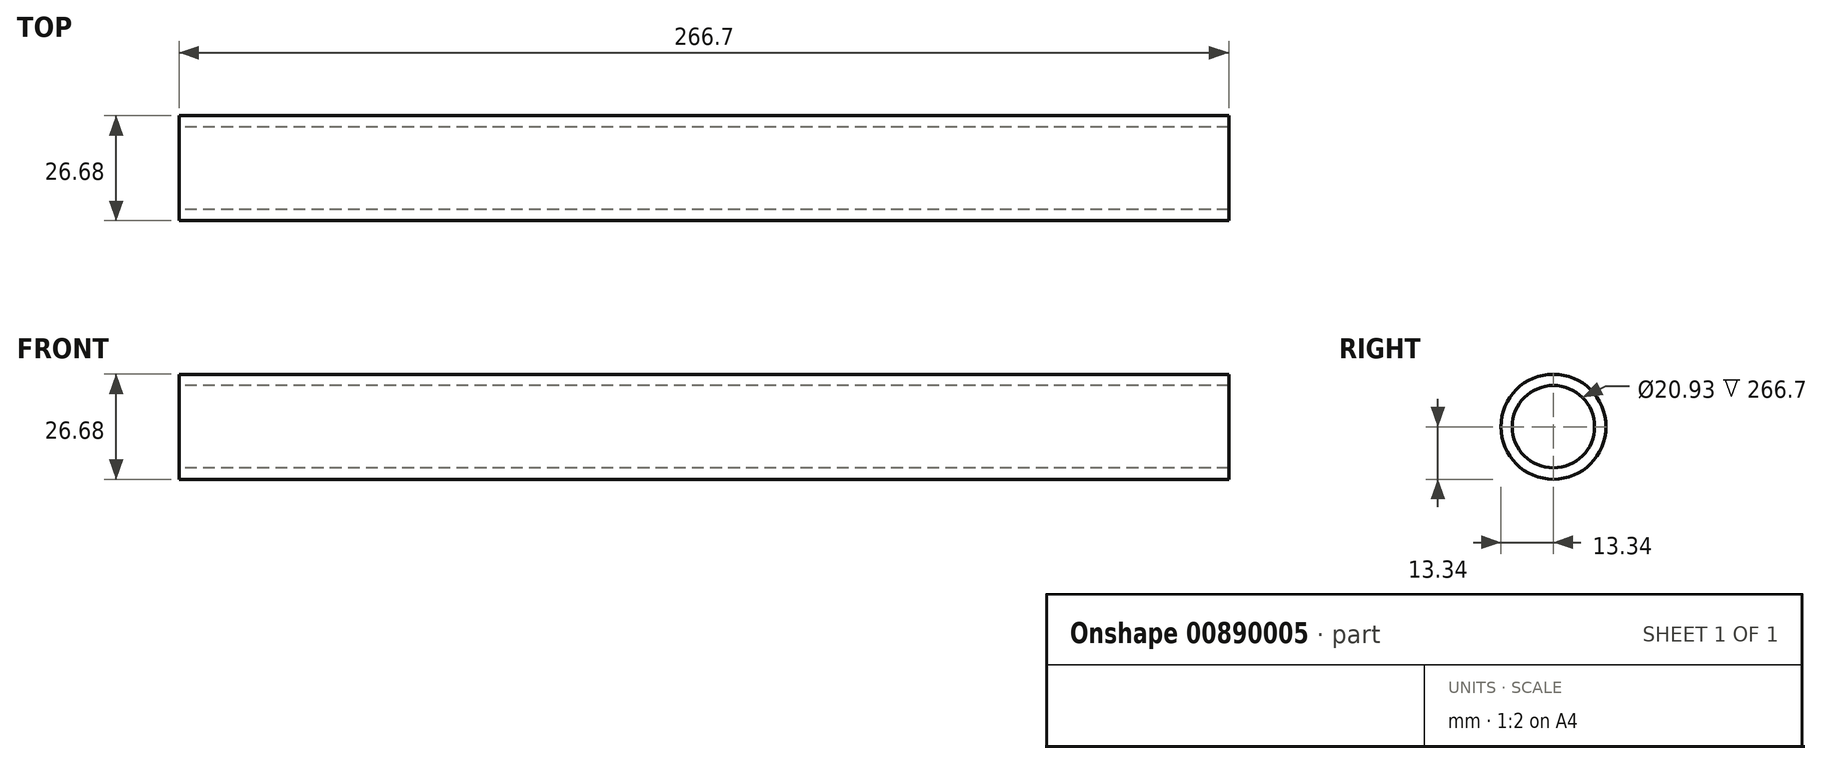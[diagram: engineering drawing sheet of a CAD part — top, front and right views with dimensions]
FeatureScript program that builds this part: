
annotation { "Feature Type Name" : "Feature", "Feature Type Description" : "" }
export const myFeature = defineFeature(function(context is Context, id is Id, definition is map)
    precondition{}
    {
        {
            var Q0;
            Q0=qCreatedBy(makeId("Right.planeOp"),FACE);
            var sketch = newSketch(context, id + "F0", { "sketchPlane" : qUnion([Q0])});
            skCircle(sketch, "E0", {"center": v(0, 0) * mm, "radius": 13.34 * mm});
            skCircle(sketch, "E1", {"center": v(0, 0) * mm, "radius": 10.46 * mm});
            skSolve(sketch);
        }
        {
            var Q0;
            Q0 = qSketchRegion(id + "F0", true);
            extrude(context, id + "F1", {"entities" : qUnion([Q0]), "depth" : 266.7 * mm, "offsetDistance" : 25.4 * mm});
        }
    });
